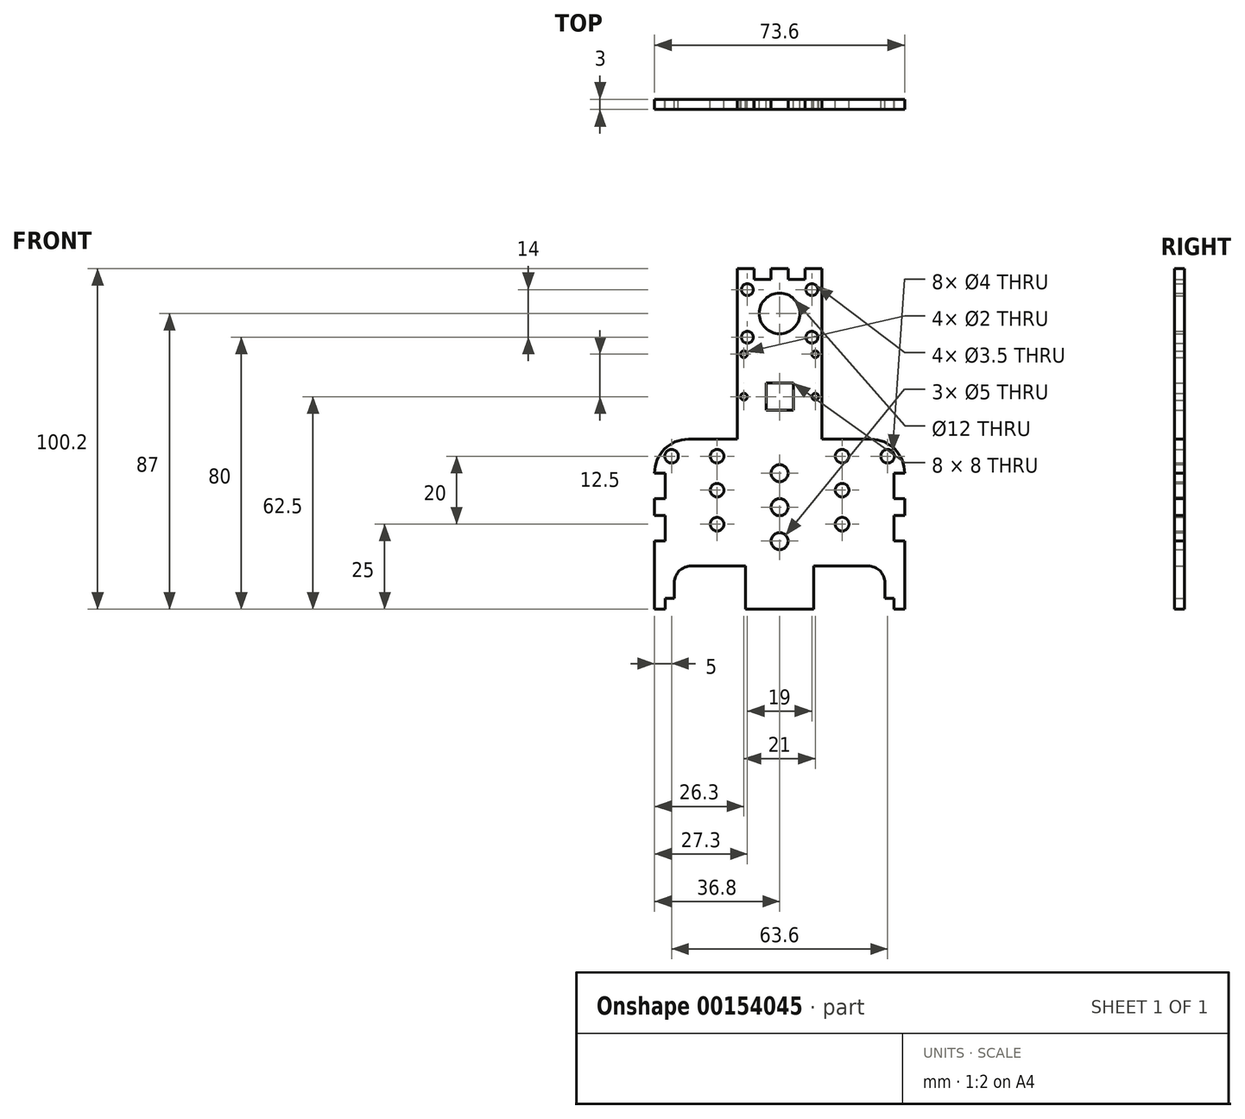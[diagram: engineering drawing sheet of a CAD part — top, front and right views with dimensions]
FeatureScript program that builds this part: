
annotation { "Feature Type Name" : "Feature", "Feature Type Description" : "" }
export const myFeature = defineFeature(function(context is Context, id is Id, definition is map)
    precondition{}
    {
        {
            var Q0;
            Q0=qCreatedBy(makeId("Front.planeOp"),FACE);
            var sketch = newSketch(context, id + "F0", { "sketchPlane" : qUnion([Q0])});
            skLineSegment(sketch, "E0.left", {"start": v(12.5, 13.5) * mm, "end": v(12.5, -13.5) * mm});
            skLineSegment(sketch, "E0.right", {"start": v(-12.5, 13.5) * mm, "end": v(-12.5, -13.5) * mm});
            skPoint(sketch, "E0.middle", {"position": v(0, 0) * mm});
            skLineSegment(sketch, "E1", {"start": v(0, 13.5) * mm, "end": v(0, -1) * mm, "construction": true});
            skPoint(sketch, "E1.endSnap0", {"position": v(0, 13.5) * mm});
            skLineSegment(sketch, "E2.bottom", {"start": v(4, 3) * mm, "end": v(-4, 3) * mm});
            skLineSegment(sketch, "E2.top", {"start": v(4, -5) * mm, "end": v(-4, -5) * mm});
            skLineSegment(sketch, "E2.left", {"start": v(4, 3) * mm, "end": v(4, -5) * mm});
            skLineSegment(sketch, "E2.right", {"start": v(-4, 3) * mm, "end": v(-4, -5) * mm});
            skPoint(sketch, "E2.middle", {"position": v(0, -1) * mm});
            skCircle(sketch, "E3", {"center": v(-10.5, 11.5) * mm, "radius": 1 * mm});
            skCircle(sketch, "E4", {"center": v(-10.5, -1) * mm, "radius": 1 * mm});
            skPoint(sketch, "E4.centerSnap0", {"position": v(-4, -1) * mm});
            skCircle(sketch, "E5.MirrorC", {"center": v(10.5, 11.5) * mm, "radius": 1 * mm});
            skCircle(sketch, "E6.MirrorC", {"center": v(10.5, -1) * mm, "radius": 1 * mm});
            skPoint(sketch, "E7.startSnap0", {"position": v(0, -5) * mm});
            skLineSegment(sketch, "E8", {"start": v(0, -13.5) * mm, "end": v(0, -33.5) * mm, "construction": true});
            skLineSegment(sketch, "E9", {"start": v(-12.5, 13.5) * mm, "end": v(-12.5, 33.5) * mm});
            skLineSegment(sketch, "E10", {"start": v(12.5, 33.5) * mm, "end": v(12.5, 13.5) * mm});
            skLineSegment(sketch, "E11", {"start": v(0, 13.5) * mm, "end": v(0, 33.5) * mm, "construction": true});
            skLineSegment(sketch, "E12", {"start": v(-12.5, 23.5) * mm, "end": v(12.5, 23.5) * mm, "construction": true});
            skCircle(sketch, "E13", {"center": v(0, 23.5) * mm, "radius": 6 * mm});
            skLineSegment(sketch, "E14", {"start": v(-12.5, 13.5) * mm, "end": v(-12.5, 16.5) * mm, "construction": true});
            skLineSegment(sketch, "E15", {"start": v(-12.5, 13.5) * mm, "end": v(-9.5, 13.5) * mm, "construction": true});
            skLineSegment(sketch, "E16", {"start": v(-9.5, 13.5) * mm, "end": v(-9.5, 33.5) * mm, "construction": true});
            skLineSegment(sketch, "E17", {"start": v(-12.5, 16.5) * mm, "end": v(12.5, 16.5) * mm, "construction": true});
            skCircle(sketch, "E18", {"center": v(-9.5, 16.5) * mm, "radius": 1.75 * mm});
            skCircle(sketch, "E19.MirrorC", {"center": v(9.5, 16.5) * mm, "radius": 1.75 * mm});
            skCircle(sketch, "E20.MirrorC", {"center": v(9.5, 30.5) * mm, "radius": 1.75 * mm});
            skCircle(sketch, "E21.MirrorC", {"center": v(-9.5, 30.5) * mm, "radius": 1.75 * mm});
            skLineSegment(sketch, "E22", {"start": v(-12.5, 33.5) * mm, "end": v(-12.5, 36.7) * mm});
            skLineSegment(sketch, "E23", {"start": v(-12.5, 36.7) * mm, "end": v(-7.5, 36.7) * mm});
            skLineSegment(sketch, "E24", {"start": v(-7.5, 36.7) * mm, "end": v(-7.5, 33.5) * mm});
            skLineSegment(sketch, "E25", {"start": v(-7.5, 33.5) * mm, "end": v(-2.5, 33.5) * mm});
            skLineSegment(sketch, "E26", {"start": v(-2.5, 33.5) * mm, "end": v(-2.5, 36.7) * mm});
            skLineSegment(sketch, "E27", {"start": v(-2.5, 36.7) * mm, "end": v(2.5, 36.7) * mm});
            skLineSegment(sketch, "E28", {"start": v(2.5, 36.7) * mm, "end": v(2.5, 33.5) * mm});
            skLineSegment(sketch, "E29", {"start": v(2.5, 33.5) * mm, "end": v(7.5, 33.5) * mm});
            skLineSegment(sketch, "E30", {"start": v(7.5, 33.5) * mm, "end": v(7.5, 36.7) * mm});
            skLineSegment(sketch, "E31", {"start": v(7.5, 36.7) * mm, "end": v(12.5, 36.7) * mm});
            skLineSegment(sketch, "E32", {"start": v(12.5, 36.7) * mm, "end": v(12.5, 33.5) * mm});
            skLineSegment(sketch, "E33.MirrorCS", {"start": v(-33.6, -60.3) * mm, "end": v(-33.6, -63.5) * mm});
            skLineSegment(sketch, "E34", {"start": v(-36.8, -63.5) * mm, "end": v(-36.8, -60.3) * mm});
            skLineSegment(sketch, "E35", {"start": v(-36.8, -63.5) * mm, "end": v(-33.6, -63.5) * mm});
            skLineSegment(sketch, "E36", {"start": v(-12.5, -13.5) * mm, "end": v(-26.8, -13.5) * mm});
            skLineSegment(sketch, "E37", {"start": v(-36.8, -31) * mm, "end": v(-36.8, -36) * mm});
            skLineSegment(sketch, "E38", {"start": v(0, -33.5) * mm, "end": v(0, -74.72) * mm, "construction": true});
            skLineSegment(sketch, "E39.MirrorCS", {"start": v(12.5, -13.5) * mm, "end": v(26.8, -13.5) * mm});
            skLineSegment(sketch, "E40.MirrorCS", {"start": v(36.8, -31) * mm, "end": v(36.8, -36) * mm});
            skLineSegment(sketch, "E41.MirrorCS", {"start": v(36.8, -63.5) * mm, "end": v(36.8, -60.3) * mm});
            skLineSegment(sketch, "E42.MirrorCS", {"start": v(36.8, -63.5) * mm, "end": v(33.6, -63.5) * mm});
            skLineSegment(sketch, "E43.MirrorCS", {"start": v(33.6, -60.3) * mm, "end": v(33.6, -63.5) * mm});
            skLineSegment(sketch, "E44", {"start": v(-10, -60.3) * mm, "end": v(-10, -63.5) * mm});
            skLineSegment(sketch, "E45", {"start": v(-10, -63.5) * mm, "end": v(10, -63.5) * mm});
            skLineSegment(sketch, "E46", {"start": v(10, -63.5) * mm, "end": v(10, -60.3) * mm});
            skLineSegment(sketch, "E47.trimOffspring", {"start": v(0, -60.3) * mm, "end": v(10, -60.3) * mm, "construction": true});
            skLineSegment(sketch, "E48", {"start": v(0, -60.3) * mm, "end": v(0, -53.3) * mm, "construction": true});
            skLineSegment(sketch, "E49.top", {"start": v(26, -50.8) * mm, "end": v(10, -50.8) * mm});
            skPoint(sketch, "E49.middle", {"position": v(0, -53.3) * mm});
            skLineSegment(sketch, "E50", {"start": v(-36.8, -13.5) * mm, "end": v(-36.8, -23.5) * mm, "construction": true});
            skLineSegment(sketch, "E51", {"start": v(-36.8, -31) * mm, "end": v(-36.8, -33.5) * mm, "construction": true});
            skLineSegment(sketch, "E52", {"start": v(-36.8, -33.5) * mm, "end": v(-36.8, -36) * mm, "construction": true});
            skCircle(sketch, "E53", {"center": v(0, -23.5) * mm, "radius": 2.5 * mm});
            skCircle(sketch, "E54", {"center": v(0, -33.5) * mm, "radius": 2.5 * mm});
            skCircle(sketch, "E55", {"center": v(0, -43.5) * mm, "radius": 2.5 * mm});
            skPoint(sketch, "E56.visualSharp", {"position": v(-36.8, -13.5) * mm});
            skArc(sketch, "E56.filletArc", {"start": v(-26.8, -13.5) * mm, "mid": v(-33.87, -16.43) * mm, "end": v(-36.8, -23.5) * mm});
            skPoint(sketch, "E57.visualSharp", {"position": v(36.8, -13.5) * mm});
            skArc(sketch, "E57.filletArc", {"start": v(36.8, -23.5) * mm, "mid": v(33.87, -16.43) * mm, "end": v(26.8, -13.5) * mm});
            skLineSegment(sketch, "E58", {"start": v(0, -60.3) * mm, "end": v(-10, -60.3) * mm, "construction": true});
            skLineSegment(sketch, "E59", {"start": v(27.8, -60.3) * mm, "end": v(27.8, -63.5) * mm, "construction": true});
            skLineSegment(sketch, "E60", {"start": v(27.8, -60.3) * mm, "end": v(27.8, -43.5) * mm, "construction": true});
            skLineSegment(sketch, "E61", {"start": v(31, -36) * mm, "end": v(31, -31) * mm, "construction": true});
            skLineSegment(sketch, "E62.MirrorCS", {"start": v(36.8, -23.5) * mm, "end": v(33.6, -23.5) * mm, "construction": true});
            skLineSegment(sketch, "E63", {"start": v(-31.8, -23.5) * mm, "end": v(-31.8, -13.5) * mm, "construction": true});
            skLineSegment(sketch, "E64", {"start": v(-36.8, -18.5) * mm, "end": v(-31.8, -18.5) * mm, "construction": true});
            skCircle(sketch, "E65", {"center": v(-31.8, -18.5) * mm, "radius": 2 * mm});
            skCircle(sketch, "E66.MirrorC", {"center": v(31.8, -18.5) * mm, "radius": 2 * mm});
            skLineSegment(sketch, "E67", {"start": v(-18.4, -23.5) * mm, "end": v(-18.4, -13.5) * mm, "construction": true});
            skLineSegment(sketch, "E68", {"start": v(-18.4, -18.5) * mm, "end": v(-31.8, -18.5) * mm, "construction": true});
            skCircle(sketch, "E69", {"center": v(-18.4, -18.5) * mm, "radius": 2 * mm});
            skCircle(sketch, "E70.MirrorC", {"center": v(18.4, -18.5) * mm, "radius": 2 * mm});
            skCircle(sketch, "E71.MirrorC", {"center": v(-18.4, -28.5) * mm, "radius": 2 * mm});
            skCircle(sketch, "E72.MirrorC", {"center": v(18.4, -28.5) * mm, "radius": 2 * mm});
            skCircle(sketch, "E73.MirrorC", {"center": v(-18.4, -38.5) * mm, "radius": 2 * mm});
            skCircle(sketch, "E74.MirrorC", {"center": v(18.4, -38.5) * mm, "radius": 2 * mm});
            skLineSegment(sketch, "E75", {"start": v(-10, -60.3) * mm, "end": v(-10, -50.8) * mm});
            skLineSegment(sketch, "E76", {"start": v(10, -60.3) * mm, "end": v(10, -50.8) * mm});
            skLineSegment(sketch, "E77.trimOffspring", {"start": v(-10, -50.8) * mm, "end": v(-26, -50.8) * mm});
            skLineSegment(sketch, "E78", {"start": v(-32.5, -60.3) * mm, "end": v(-33.6, -60.3) * mm});
            skLineSegment(sketch, "E79", {"start": v(32.5, -60.3) * mm, "end": v(33.6, -60.3) * mm});
            skLineSegment(sketch, "E80", {"start": v(0, -60.3) * mm, "end": v(33.6, -60.3) * mm, "construction": true});
            skLineSegment(sketch, "E81", {"start": v(33.6, -60.3) * mm, "end": v(33.6, -3.55) * mm, "construction": true});
            skLineSegment(sketch, "E82.bottom", {"start": v(33.6, -43.5) * mm, "end": v(36.8, -43.5) * mm});
            skLineSegment(sketch, "E82.top", {"start": v(33.6, -36) * mm, "end": v(36.8, -36) * mm});
            skLineSegment(sketch, "E82.left", {"start": v(33.6, -43.5) * mm, "end": v(33.6, -36) * mm});
            skLineSegment(sketch, "E83", {"start": v(31, -31) * mm, "end": v(33.6, -31) * mm, "construction": true});
            skLineSegment(sketch, "E84.bottom", {"start": v(33.6, -31) * mm, "end": v(36.8, -31) * mm});
            skLineSegment(sketch, "E84.top", {"start": v(33.6, -23.5) * mm, "end": v(36.8, -23.5) * mm});
            skLineSegment(sketch, "E84.left", {"start": v(33.6, -31) * mm, "end": v(33.6, -23.5) * mm});
            skLineSegment(sketch, "E85.trimOffspring", {"start": v(33.6, -23.5) * mm, "end": v(36.8, -23.5) * mm, "construction": true});
            skPoint(sketch, "E86.end.orphan", {"position": v(27.8, -36) * mm});
            skLineSegment(sketch, "E87.trimOffspring", {"start": v(31, -43.5) * mm, "end": v(36.8, -43.5) * mm, "construction": true});
            skPoint(sketch, "E88.end.orphan", {"position": v(27.8, -31) * mm});
            skLineSegment(sketch, "E89.trimOffspring", {"start": v(36.8, -43.5) * mm, "end": v(36.8, -60.3) * mm});
            skLineSegment(sketch, "E90.MirrorCS", {"start": v(-33.6, -31) * mm, "end": v(-36.8, -31) * mm});
            skLineSegment(sketch, "E91.top", {"start": v(-33.6, -23.5) * mm, "end": v(-36.8, -23.5) * mm});
            skLineSegment(sketch, "E91.left", {"start": v(-33.6, -31) * mm, "end": v(-33.6, -23.5) * mm});
            skLineSegment(sketch, "E92.MirrorCS", {"start": v(-33.6, -36) * mm, "end": v(-36.8, -36) * mm});
            skLineSegment(sketch, "E93.top", {"start": v(-33.6, -43.5) * mm, "end": v(-36.8, -43.5) * mm});
            skLineSegment(sketch, "E93.left", {"start": v(-33.6, -36) * mm, "end": v(-33.6, -43.5) * mm});
            skLineSegment(sketch, "E94.trimOffspring", {"start": v(-36.8, -43.5) * mm, "end": v(-36.8, -60.3) * mm});
            skLineSegment(sketch, "E95", {"start": v(-32.5, -60.3) * mm, "end": v(-31, -60.3) * mm});
            skLineSegment(sketch, "E96", {"start": v(-31, -60.3) * mm, "end": v(-31, -55.8) * mm});
            skLineSegment(sketch, "E97.MirrorCS", {"start": v(31, -60.3) * mm, "end": v(31, -55.8) * mm});
            skLineSegment(sketch, "E98", {"start": v(31, -60.3) * mm, "end": v(32.5, -60.3) * mm});
            skPoint(sketch, "E99.visualSharp", {"position": v(-31, -50.8) * mm});
            skArc(sketch, "E99.filletArc", {"start": v(-26, -50.8) * mm, "mid": v(-29.54, -52.26) * mm, "end": v(-31, -55.8) * mm});
            skPoint(sketch, "E100.visualSharp", {"position": v(31, -50.8) * mm});
            skArc(sketch, "E100.filletArc", {"start": v(31, -55.8) * mm, "mid": v(29.54, -52.26) * mm, "end": v(26, -50.8) * mm});
            skSolve(sketch);
        }
        {
            var Q0;
            Q0=qSketchRegion(id+"F0",true);
            extrude(context, id + "F1", {"entities" : qUnion([Q0]), "endBound" : BoundingType.SYMMETRIC, "depth" : 3 * mm});
        }
    });
